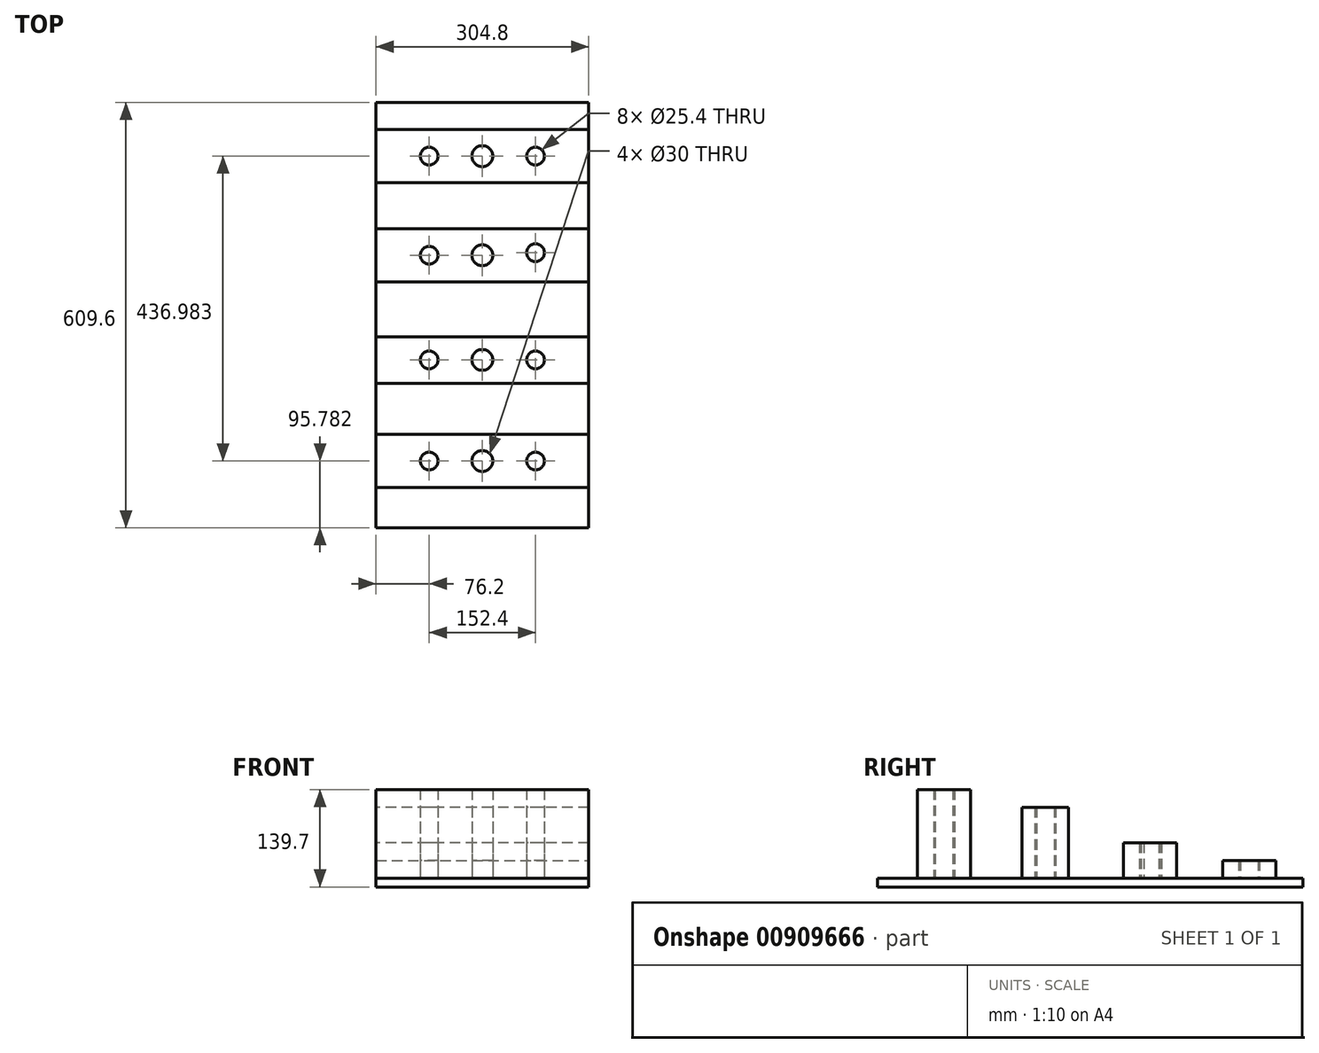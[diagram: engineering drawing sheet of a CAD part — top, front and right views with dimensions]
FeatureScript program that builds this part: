
annotation { "Feature Type Name" : "Feature", "Feature Type Description" : "" }
export const myFeature = defineFeature(function(context is Context, id is Id, definition is map)
    precondition{}
    {
        {
            var Q0;
            Q0=qCreatedBy(makeId("Top.planeOp"),FACE);
            var sketch = newSketch(context, id + "F0", { "sketchPlane" : qUnion([Q0])});
            skLineSegment(sketch, "E0.bottom", {"start": v(152.4, 304.8) * mm, "end": v(-152.4, 304.8) * mm});
            skLineSegment(sketch, "E0.top", {"start": v(152.4, -304.8) * mm, "end": v(-152.4, -304.8) * mm});
            skLineSegment(sketch, "E0.left", {"start": v(152.4, 304.8) * mm, "end": v(152.4, -304.8) * mm});
            skLineSegment(sketch, "E0.right", {"start": v(-152.4, 304.8) * mm, "end": v(-152.4, -304.8) * mm});
            skPoint(sketch, "E0.middle", {"position": v(0, 0) * mm});
            skSolve(sketch);
        }
        {
            var Q0;
            Q0 = qSketchRegion(id + "F0", true);
            extrude(context, id + "F1", {"entities" : qUnion([Q0]), "oppositeDirection" : true, "depth" : 12.7 * mm, "offsetDistance" : 25 * mm});
        }
        {
            var Q0;
            Q0=makeQuery(id+"F1.opExtrude","CAP_FACE",FACE,{"disambiguationData":[OSD([sQuery(id+"F0.wireOp",EDGE,"E0.bottom"),sQuery(id+"F0.wireOp",EDGE,"E0.top"),sQuery(id+"F0.wireOp",EDGE,"E0.left"),sQuery(id+"F0.wireOp",EDGE,"E0.right")])],"isStart":true});
            var sketch = newSketch(context, id + "F2", { "sketchPlane" : qUnion([Q0])});
            skLineSegment(sketch, "E1.bottom", {"start": v(152.4, -170.92) * mm, "end": v(-152.4, -170.92) * mm});
            skLineSegment(sketch, "E1.top", {"start": v(152.4, -247.12) * mm, "end": v(-152.4, -247.12) * mm});
            skLineSegment(sketch, "E1.left", {"start": v(152.4, -170.92) * mm, "end": v(152.4, -247.12) * mm});
            skLineSegment(sketch, "E1.right", {"start": v(-152.4, -170.92) * mm, "end": v(-152.4, -247.12) * mm});
            skPoint(sketch, "E1.middle", {"position": v(0, -209.02) * mm});
            skCircle(sketch, "E2", {"center": v(-76.2, -209.02) * mm, "radius": 12.7 * mm});
            skCircle(sketch, "E3", {"center": v(76.2, -209.02) * mm, "radius": 12.7 * mm});
            skCircle(sketch, "E4", {"center": v(0, -209.02) * mm, "radius": 15 * mm});
            skSolve(sketch);
        }
        {
            var Q0;
            Q0 = qSketchRegion(id + "F2", true);
            extrude(context, id + "F3", {"entities" : qUnion([Q0]), "depth" : 127 * mm, "offsetDistance" : 25 * mm});
        }
        {
            var Q0;
            Q0=makeQuery(id+"F1.opExtrude","CAP_FACE",FACE,{"disambiguationData":[OSD([sQuery(id+"F0.wireOp",EDGE,"E0.bottom"),sQuery(id+"F0.wireOp",EDGE,"E0.top"),sQuery(id+"F0.wireOp",EDGE,"E0.left"),sQuery(id+"F0.wireOp",EDGE,"E0.right")])],"isStart":true});
            var sketch = newSketch(context, id + "F4", { "sketchPlane" : qUnion([Q0])});
            skLineSegment(sketch, "E5.bottom", {"start": v(152.4, -30.76) * mm, "end": v(-152.4, -30.76) * mm});
            skLineSegment(sketch, "E5.top", {"start": v(152.4, -97.44) * mm, "end": v(-152.4, -97.44) * mm});
            skLineSegment(sketch, "E5.left", {"start": v(152.4, -30.76) * mm, "end": v(152.4, -97.44) * mm});
            skLineSegment(sketch, "E5.right", {"start": v(-152.4, -30.76) * mm, "end": v(-152.4, -97.44) * mm});
            skPoint(sketch, "E5.middle", {"position": v(0, -64.1) * mm});
            skCircle(sketch, "E6", {"center": v(-76.2, -64.1) * mm, "radius": 12.7 * mm});
            skCircle(sketch, "E7", {"center": v(76.2, -64.1) * mm, "radius": 12.7 * mm});
            skCircle(sketch, "E8", {"center": v(0, -64.1) * mm, "radius": 15 * mm});
            skSolve(sketch);
        }
        {
            var Q0;
            Q0 = qSketchRegion(id + "F4", true);
            extrude(context, id + "F5", {"entities" : qUnion([Q0]), "depth" : 101.6 * mm, "offsetDistance" : 25 * mm});
        }
        {
            var Q0;
            Q0=makeQuery(id+"F1.opExtrude","CAP_FACE",FACE,{"disambiguationData":[OSD([sQuery(id+"F0.wireOp",EDGE,"E0.bottom"),sQuery(id+"F0.wireOp",EDGE,"E0.top"),sQuery(id+"F0.wireOp",EDGE,"E0.left"),sQuery(id+"F0.wireOp",EDGE,"E0.right")])],"isStart":true});
            var sketch = newSketch(context, id + "F6", { "sketchPlane" : qUnion([Q0])});
            skLineSegment(sketch, "E9.bottom", {"start": v(152.4, 123.95) * mm, "end": v(-152.4, 123.95) * mm});
            skLineSegment(sketch, "E9.top", {"start": v(152.4, 47.75) * mm, "end": v(-152.4, 47.75) * mm});
            skLineSegment(sketch, "E9.left", {"start": v(152.4, 123.95) * mm, "end": v(152.4, 47.75) * mm});
            skLineSegment(sketch, "E9.right", {"start": v(-152.4, 123.95) * mm, "end": v(-152.4, 47.75) * mm});
            skPoint(sketch, "E9.middle", {"position": v(0, 85.85) * mm});
            skCircle(sketch, "E10", {"center": v(-76.2, 85.85) * mm, "radius": 12.7 * mm});
            skCircle(sketch, "E11", {"center": v(76.2, 89.57) * mm, "radius": 12.7 * mm});
            skCircle(sketch, "E12", {"center": v(0, 85.85) * mm, "radius": 15 * mm});
            skSolve(sketch);
        }
        {
            var Q0;
            Q0 = qSketchRegion(id + "F6", true);
            extrude(context, id + "F7", {"entities" : qUnion([Q0]), "depth" : 50.8 * mm, "offsetDistance" : 25 * mm});
        }
        {
            var Q0;
            Q0=makeQuery(id+"F1.opExtrude","CAP_FACE",FACE,{"disambiguationData":[OSD([sQuery(id+"F0.wireOp",EDGE,"E0.bottom"),sQuery(id+"F0.wireOp",EDGE,"E0.top"),sQuery(id+"F0.wireOp",EDGE,"E0.left"),sQuery(id+"F0.wireOp",EDGE,"E0.right")])],"isStart":true});
            var sketch = newSketch(context, id + "F8", { "sketchPlane" : qUnion([Q0])});
            skLineSegment(sketch, "E13.bottom", {"start": v(-152.4, 266.07) * mm, "end": v(152.4, 266.07) * mm});
            skLineSegment(sketch, "E13.top", {"start": v(-152.4, 189.87) * mm, "end": v(152.4, 189.87) * mm});
            skLineSegment(sketch, "E13.left", {"start": v(-152.4, 266.07) * mm, "end": v(-152.4, 189.87) * mm});
            skLineSegment(sketch, "E13.right", {"start": v(152.4, 266.07) * mm, "end": v(152.4, 189.87) * mm});
            skPoint(sketch, "E13.middle", {"position": v(0, 227.97) * mm});
            skCircle(sketch, "E14", {"center": v(-76.2, 227.97) * mm, "radius": 12.7 * mm});
            skCircle(sketch, "E15", {"center": v(76.2, 227.97) * mm, "radius": 12.7 * mm});
            skCircle(sketch, "E16", {"center": v(0, 227.97) * mm, "radius": 15 * mm});
            skSolve(sketch);
        }
        {
            var Q0;
            Q0 = qSketchRegion(id + "F8", true);
            extrude(context, id + "F9", {"entities" : qUnion([Q0]), "depth" : 25.4 * mm, "offsetDistance" : 25 * mm});
        }
    });
